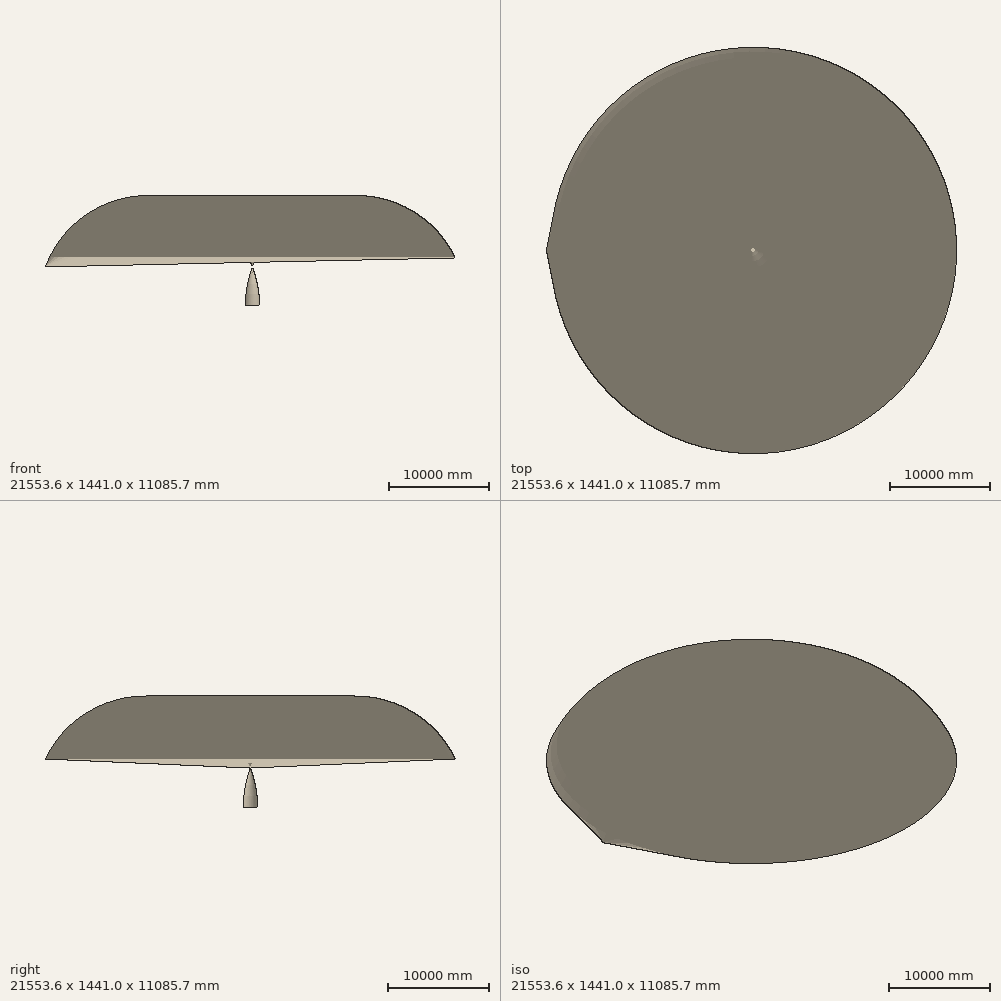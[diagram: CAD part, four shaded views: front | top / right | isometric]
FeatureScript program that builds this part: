
annotation { "Feature Type Name" : "Feature", "Feature Type Description" : "" }
export const myFeature = defineFeature(function(context is Context, id is Id, definition is map)
    precondition{}
    {
        {
            var Q0;
            Q0=qCreatedBy(makeId("Right.planeOp"),FACE);
            var sketch = newSketch(context, id + "F0", { "sketchPlane" : qUnion([Q0])});
            skLineSegment(sketch, "E0.bottom", {"start": v(0, 0) * mm, "end": v(720.6, 0) * mm});
            skLineSegment(sketch, "E0.left", {"start": v(0, 0) * mm, "end": v(0, 867.02) * mm});
            skLineSegment(sketch, "E1", {"start": v(0, 867.02) * mm, "end": v(0, 3889.58) * mm});
            skArc(sketch, "E2", {"start": v(720.48, 0) * mm, "mid": v(534.31, 1977.03) * mm, "end": v(0, 3889.58) * mm});
            skLineSegment(sketch, "E3.bottom", {"start": v(0, 0) * mm, "end": v(241.3, 0) * mm});
            skLineSegment(sketch, "E3.top", {"start": v(0, 1574.8) * mm, "end": v(241.3, 1574.8) * mm});
            skLineSegment(sketch, "E3.left", {"start": v(0, 0) * mm, "end": v(0, 1574.8) * mm});
            skLineSegment(sketch, "E3.right", {"start": v(241.3, 0) * mm, "end": v(241.3, 1574.8) * mm});
            skLineSegment(sketch, "E4.bottom", {"start": v(241.3, 783.82) * mm, "end": v(241.3, 783.82) * mm});
            skLineSegment(sketch, "E4.top", {"start": v(241.3, 3180.64) * mm, "end": v(241.3, 3180.64) * mm});
            skLineSegment(sketch, "E4.left", {"start": v(241.3, 783.82) * mm, "end": v(241.3, 1574.8) * mm});
            skSolve(sketch);
        }
        {
            var Q0;
            Q0=makeQuery(id+"F0.imprint","IMPRINT",FACE,{"disambiguationData":[TD([[makeQuery(id+"F0.imprint","IMPRINT",EDGE,{"derivedFrom":sQuery(id+"F0.wireOp",EDGE,"E0.bottom")}),1.0]])]});
            var Q1;
            Q1=sQuery(id+"F0.wireOp",EDGE,"E1");
            revolve(context, id + "F1", {"entities" : qUnion([Q0]), "axis" : qUnion([Q1]), "revolveType" : RevolveType.FULL});
        }
    });
